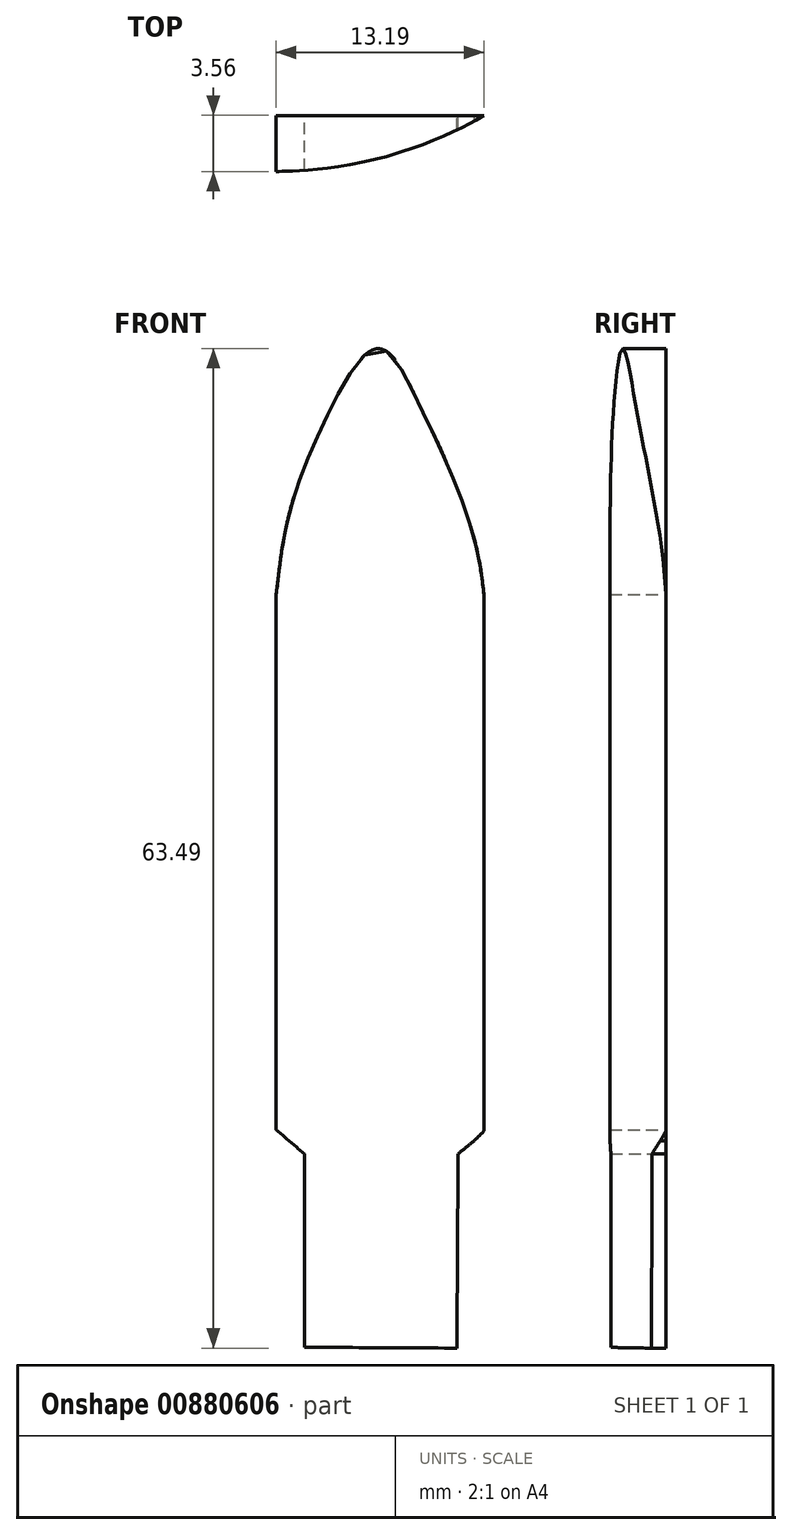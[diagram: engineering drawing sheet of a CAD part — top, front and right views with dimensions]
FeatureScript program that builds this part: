
annotation { "Feature Type Name" : "Feature", "Feature Type Description" : "" }
export const myFeature = defineFeature(function(context is Context, id is Id, definition is map)
    precondition{}
    {
        {
            var Q0;
            Q0=qCreatedBy(makeId("Front.planeOp"),FACE);
            cPlane(context, id + "F0", {"entities" : qUnion([Q0]), "cplaneType" : CPlaneType.OFFSET, "offset" : 3.56 * mm, "oppositeDirection" : true, "width" : 152.4 * mm, "height" : 152.4 * mm});
        }
        {
            var Q0;
            Q0=qCreatedBy(id+"F0.planeOp",FACE);
            var sketch = newSketch(context, id + "F1", { "sketchPlane" : qUnion([Q0])});
            skLineSegment(sketch, "E0", {"start": v(-4.76, -3.72) * mm, "end": v(-4.76, 30.28) * mm});
            skFitSpline(sketch, "E1", {"points": [v(-4.76, 30.28) * mm, v(-3.95, 35.38) * mm, v(-1.45, 41.8) * mm, v(1.85, 45.9) * mm, v(4.3, 42.4) * mm, v(5.46, 40) * mm, v(7.7, 34.26) * mm, v(8.43, 30.28) * mm], "startDerivative": vector(3.8, 34.13) * mm, "endDerivative": vector(3.36, -27.87) * mm});
            skLineSegment(sketch, "E2", {"start": v(8.43, 30.28) * mm, "end": v(8.43, -3.8) * mm});
            skLineSegment(sketch, "E3", {"start": v(-4.76, -3.72) * mm, "end": v(-2.98, -5.24) * mm});
            skLineSegment(sketch, "E4", {"start": v(-2.98, -5.24) * mm, "end": v(-2.98, -17.52) * mm});
            skLineSegment(sketch, "E5", {"start": v(-2.98, -17.52) * mm, "end": v(6.71, -17.58) * mm});
            skLineSegment(sketch, "E6", {"start": v(6.71, -17.58) * mm, "end": v(6.79, -5.24) * mm});
            skLineSegment(sketch, "E7", {"start": v(6.79, -5.24) * mm, "end": v(7.82, -4.4) * mm});
            skLineSegment(sketch, "E8", {"start": v(7.82, -4.4) * mm, "end": v(8.43, -3.8) * mm});
            skSolve(sketch);
        }
        {
            var Q0;
            Q0=makeQuery(id+"F1.imprint","IMPRINT",FACE,{"disambiguationData":[TD([[makeQuery(id+"F1.imprint","IMPRINT",EDGE,{"derivedFrom":sQuery(id+"F1.wireOp",EDGE,"E0")}),-1.0]])]});
            extrude(context, id + "F2", {"entities" : qUnion([Q0]), "depth" : 3.56 * mm, "offsetDistance" : 25.4 * mm});
        }
        {
            var Q0;
            Q0=makeQuery(id+"F2.opExtrude","CAP_EDGE",EDGE,{"disambiguationData":[OSD([sQuery(id+"F1.wireOp",EDGE,"E2")])],"isStart":false});
            fillet(context, id + "F3", {"entities" : qUnion([Q0]), "radius" : 26.37 * mm, "tangentPropagation" : true, "allowEdgeOverflow" : false});
        }
    });
